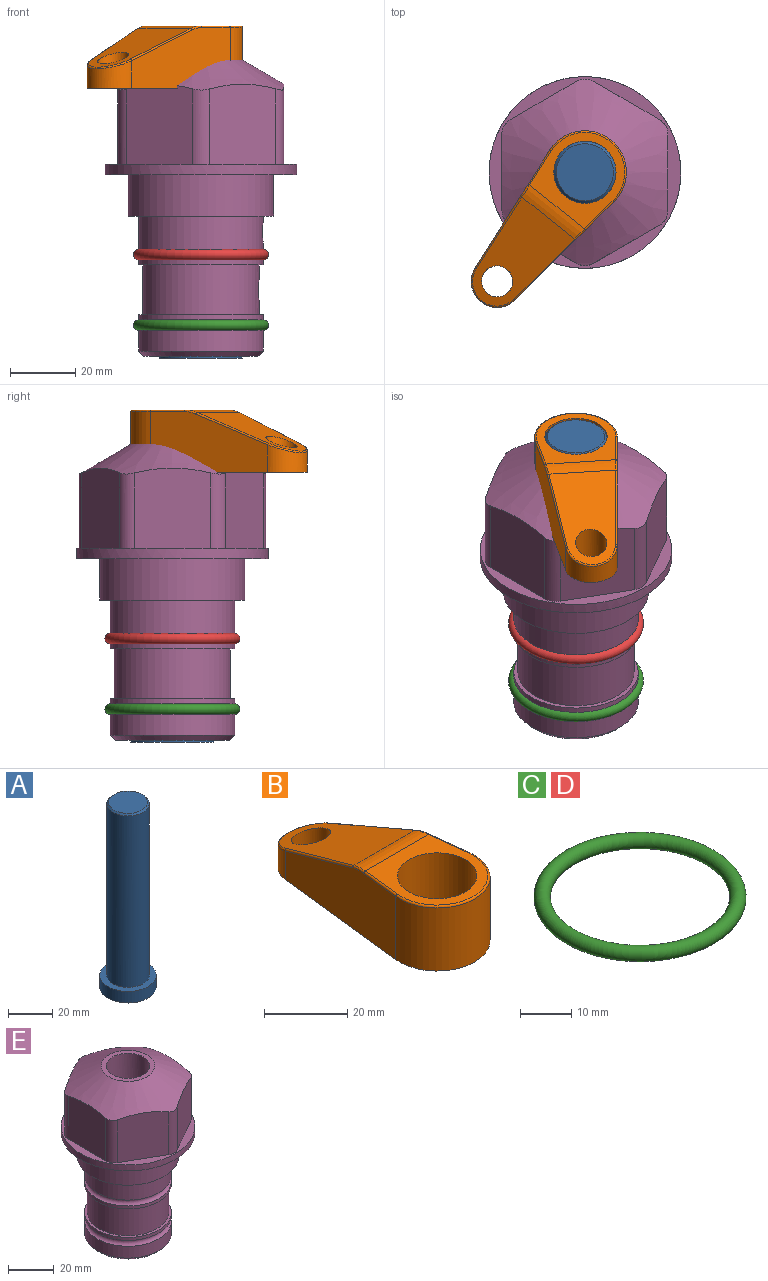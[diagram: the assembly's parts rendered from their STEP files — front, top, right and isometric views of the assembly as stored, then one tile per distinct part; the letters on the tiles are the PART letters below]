
ASSEMBLY  parts=5 mates=3
PART A: 6 faces, bbox 25.4x25.4x101.6 mm
  f0: plane 17.46x17.46mm, normal (0,0,1), area 239.5mm2, adj f5
  f1: plane 25.4x25.4mm, normal (0,0,-1), area 506.7mm2, adj f2
  f2: cylinder r=12.7mm len=25.4mm, axis (0,0,1), area 506.7mm2, adj f1,f3
  f3: plane 25.4x25.4mm, normal (0,0,1), area 221.7mm2, adj f2,f4
  f4: cylinder r=9.53mm len=94.46mm, axis (0,0,1), area 5653mm2, adj f3,f5
  f5: cone r=8.73mm half-angle=45deg, axis (0,0,-1), area 64.4mm2, adj f0,f4
PART B: 44 faces, bbox 27.5x64.5x19.1 mm
  f0: plane 2.3x0.95mm, normal (0,0,-1), area 1mm2, adj f25,f30,f34
  f1: plane 63.5x25.4mm, normal (0,0,-1), area 561.7mm2, adj f2,f3,f4,f5,f6,f7,f19,f20
  f2: cylinder r=12.7mm len=25.4mm, axis (0,0,-1), area 792.2mm2, adj f1,f3,f5,f13
  f3: plane 42.33x18.54mm, normal (0.99,0.11,0), area 647mm2, adj f1,f2,f4,f11,f12,f14
  f4: cylinder r=7.94mm len=15.78mm, axis (0,0,-1), area 158.6mm2, adj f1,f3,f5,f16
  f5: plane 42.33x18.54mm, normal (-0.99,0.11,0), area 647mm2, adj f1,f2,f4,f15,f17,f18
  f6: cylinder r=9.53mm len=19.05mm, axis (0,0,-1), area 1140.1mm2, adj f1,f8
  f7: cylinder r=4.76mm len=10.98mm, axis (0,0,-1), area 276.1mm2, adj f1,f9
  f8: plane 25.83x24.38mm, normal (0,0,1), area 262.2mm2, adj f6,f10,f11,f13,f15
  f9: plane 32.49x20.55mm, normal (0,0.34,0.94), area 489.9mm2, adj f7,f10,f14,f16,f18
  f10: cylinder r=12.7mm len=21.49mm, axis (-1,0,0), area 93.2mm2, adj f8,f9,f12,f17
  f11: cylinder r=0.51mm len=12.34mm, axis (0.11,-0.99,0), area 9.9mm2, adj f3,f8,f12,f13
  f12: bspline ~7.62x1.64mm, area 3.5mm2, adj f3,f10,f11,f14
  f13: torus R=12.19mm, axis (0,0,1), area 33.6mm2, adj f2,f8,f11,f15
  f14: cylinder r=0.51mm len=26.01mm, axis (0.1,-0.93,0.34), area 21.6mm2, adj f3,f9,f12,f16
  f15: cylinder r=0.51mm len=12.34mm, axis (0.11,0.99,0), area 9.9mm2, adj f5,f8,f13,f17
  f16: bspline ~15.78x7.05mm, area 15.7mm2, adj f4,f9,f14,f18
  f17: bspline ~7.62x1.64mm, area 3.5mm2, adj f5,f10,f15,f18
  f18: cylinder r=0.51mm len=26.01mm, axis (0.1,0.93,-0.34), area 21.6mm2, adj f5,f9,f16,f17
  f19: plane 21.6x14.29mm, normal (-0.99,-0.11,0), area 242.6mm2, adj f1,f26,f28,f34,f36,f38
  f20: plane 21.6x14.29mm, normal (0.99,-0.11,0), area 242.6mm2, adj f1,f27,f29,f37,f39,f41
  f21: cylinder r=12.7mm len=14.29mm, axis (0,0,-1), area 173.2mm2, adj f1,f26,f27,f30,f31,f33
  f22: cylinder r=7.94mm len=7.63mm, axis (0,0,-1), area 53.8mm2, adj f1,f28,f29,f42
  f23: plane 2.3x0.95mm, normal (0,0,-1), area 1mm2, adj f25,f33,f37
  f24: plane 17.94x12.32mm, normal (0,-0.34,-0.94), area 191.2mm2, adj f25,f38,f41,f42
  f25: cylinder r=9.53mm len=12.93mm, axis (-1,0,0), area 37.5mm2, adj f0,f23,f24,f31,f36,f39
  f26: cylinder r=1.59mm len=14.29mm, axis (0,0,-1), area 49mm2, adj f1,f19,f21,f32
  f27: cylinder r=1.59mm len=14.29mm, axis (0,0,-1), area 49mm2, adj f1,f20,f21,f35
  f28: cylinder r=1.59mm len=7.28mm, axis (0,0,-1), area 22.1mm2, adj f1,f19,f22,f40
  f29: cylinder r=1.59mm len=7.28mm, axis (0,0,-1), area 22.1mm2, adj f1,f20,f22,f43
  f30: torus R=14.29mm, axis (0,0,1), area 5.8mm2, adj f0,f21,f31,f32
  f31: bspline ~11.06x2.73mm, area 20.8mm2, adj f21,f25,f30,f33
  f32: sphere r=1.59mm, area 5.4mm2, adj f26,f30,f34
  f33: torus R=14.29mm, axis (0,0,1), area 5.8mm2, adj f21,f23,f31,f35
  f34: cylinder r=1.59mm len=1.68mm, axis (-0.11,0.99,0), area 2.4mm2, adj f0,f19,f32,f36
  f35: sphere r=1.59mm, area 5.4mm2, adj f27,f33,f37
  f36: bspline ~5.82x2.33mm, area 7.7mm2, adj f19,f25,f34,f38
  f37: cylinder r=1.59mm len=1.68mm, axis (0.11,0.99,0), area 2.4mm2, adj f20,f23,f35,f39
  f38: cylinder r=1.59mm len=18.33mm, axis (0.1,-0.93,0.34), area 46.7mm2, adj f19,f24,f36,f40
  f39: bspline ~5.82x2.33mm, area 7.7mm2, adj f20,f25,f37,f41
  f40: sphere r=1.59mm, area 3.6mm2, adj f28,f38,f42
  f41: cylinder r=1.59mm len=18.33mm, axis (0.1,0.93,-0.34), area 46.7mm2, adj f20,f24,f39,f43
  f42: bspline ~8.31x1.84mm, area 15.3mm2, adj f22,f24,f40,f43
  f43: sphere r=1.59mm, area 3.6mm2, adj f29,f41,f42
PART C: 1 faces, bbox 44.7x44.7x3.2 mm
  f0: torus R=19.05mm, axis (0,0,1), area 1193.9mm2
PART D: same geometry as C
PART E: 36 faces, bbox 58.7x58.7x91.2 mm
  f0: cylinder r=17.78mm len=35.56mm, axis (0,0,1), area 1670.8mm2, adj f23,f24,f31
  f1: cylinder r=19.05mm len=38.1mm, axis (0,0,1), area 1191.9mm2, adj f26,f27,f30
  f2: plane 58.66x58.66mm, normal (0,0,-1), area 1150.6mm2, adj f3,f28
  f3: cylinder r=29.33mm len=58.66mm, axis (0,0,-1), area 585.1mm2, adj f2,f4
  f4: plane 58.66x58.66mm, normal (0,0,1), area 475.9mm2, adj f3,f5,f6,f7,f8,f9,f10,f11
  f5: plane 24.5x20.32mm, normal (-0.5,0.87,0), area 562.8mm2, adj f4,f15,f16,f17
  f6: plane 24.5x20.32mm, normal (0.5,0.87,0), area 562.8mm2, adj f4,f14,f15,f17
  f7: plane 24.5x23.48mm, normal (1,0,0), area 562.8mm2, adj f4,f13,f14,f17
  f8: plane 24.5x20.32mm, normal (0.5,-0.87,0), area 562.8mm2, adj f4,f12,f13,f17
  f9: plane 24.5x20.32mm, normal (-0.5,-0.87,0), area 562.8mm2, adj f4,f11,f12,f17
  f10: plane 24.5x23.48mm, normal (-1,0,0), area 562.8mm2, adj f4,f11,f16,f17
  f11: cylinder r=5.08mm len=23.01mm, axis (0,0,-1), area 121.2mm2, adj f4,f9,f10,f17
  f12: cylinder r=5.08mm len=23.01mm, axis (0,0,-1), area 121.2mm2, adj f4,f8,f9,f17
  f13: cylinder r=5.08mm len=23.01mm, axis (0,0,-1), area 121.2mm2, adj f4,f7,f8,f17
  f14: cylinder r=5.08mm len=23.01mm, axis (0,0,-1), area 121.2mm2, adj f4,f6,f7,f17
  f15: cylinder r=5.08mm len=23.01mm, axis (0,0,-1), area 121.2mm2, adj f4,f5,f6,f17
  f16: cylinder r=5.08mm len=23.01mm, axis (0,0,-1), area 121.2mm2, adj f4,f5,f10,f17
  f17: cone r=11.73mm half-angle=60deg, axis (0,0,-1), area 2071.8mm2, adj f5,f6,f7,f8,f9,f10,f11,f12
  f18: plane 23.46x23.46mm, normal (0,0,1), area 147.4mm2, adj f17,f35
  f19: plane 34.93x34.93mm, normal (0,0,-1), area 958mm2, adj f29
  f20: cylinder r=19.05mm len=38.1mm, axis (0,0,1), area 760.1mm2, adj f21,f29
  f21: torus R=19.05mm, axis (0,0,1), area 565.3mm2, adj f20,f22
  f22: cylinder r=19.05mm len=38.1mm, axis (0,0,1), area 190mm2, adj f21,f23
  f23: plane 38.1x38.1mm, normal (0,0,1), area 146.9mm2, adj f0,f22
  f24: plane 38.1x38.1mm, normal (0,0,-1), area 146.9mm2, adj f0,f25
  f25: cylinder r=19.05mm len=38.1mm, axis (0,0,1), area 190mm2, adj f24,f26
  f26: torus R=19.05mm, axis (0,0,1), area 565.3mm2, adj f1,f25
  f27: plane 44.45x44.45mm, normal (0,0,-1), area 411.7mm2, adj f1,f28
  f28: cylinder r=22.23mm len=44.45mm, axis (0,0,1), area 1773.5mm2, adj f2,f27
  f29: cone r=19.05mm half-angle=45deg, axis (0,0,1), area 257.5mm2, adj f19,f20
  f30: cylinder r=3.17mm len=6.75mm, axis (-1,0,0), area 128mm2, adj f1,f33
  f31: cylinder r=3.17mm len=6.35mm, axis (-1,0,0), area 102.5mm2, adj f0,f33
  f32: plane 25.4x25.4mm, normal (0,0,1), area 506.7mm2, adj f33
  f33: cylinder r=12.7mm len=66.42mm, axis (0,0,-1), area 5236.2mm2, adj f30,f31,f32,f34
  f34: cone r=9.53mm half-angle=30deg, axis (0,0,-1), area 443.4mm2, adj f33,f35
  f35: cylinder r=9.53mm len=19.05mm, axis (0,0,-1), area 849mm2, adj f18,f34
PLACE A rot(axis=(0,0,-1),128.8deg) t=(0,0,-28.21)mm
PLACE B rot(axis=(0,0,1),141.2deg) t=(0,0,26.4)mm
PLACE C t=(0,0,-21.59)mm
PLACE D at identity
PLACE E at identity fixed
MATE fastened C.f0 <-> E.f0  axis (0,0,1) through (0,0,-46.1)mm
MATE cylindrical A.f2 <-> E.f0  axis (0,0,1) through (0,0,-2.57)mm
MATE fastened B.f2 <-> A.f2  axis (0,0,1) through (0,0,45.45)mm
